# Revit family: Celite_City_Lavatório com Coluna Suspensa_20001
name_source: partatom
category: Plumbing Fixtures
revit_build: Autodesk Revit MEP 2014 (Build: 20131024_2115(x64)
units: mm (PartAtom-declared; Revit-internal decimal feet)

## types (4) — shared parameters
Assembly Code = D2010400
Celite: Categoria = Linhas completas
Celite: Código = 20001
Celite: Desenho Técnico = http://www.celite.com.br
Celite: Fabricante = Celite
Celite: Linha = City
Celite: Link do Produto = http://www.celite.com.br
Celite: Norma = ABNT NBR 15097-1: 2011 - Requisitos e métodos de ensaio
Celite: Produto = Louças
Celite: Tipo = Lavatórios com coluna
Celite: Versão = Autodesk Revit MEP 2014
Desenvolvido por = ofcdesk
Diâmetro Ponto de Esgoto = 40 mm
Manufacturer = Celite
Model = 20001
Raio Ponto de Esgoto = 20 mm
Selo de Qualidade ofcdesk = Standard
URL = http://www.celite.com.br
WFU = 2
zero-valued in all types: CWFU, Default Elevation, HWFU

## per-type parameters (varying)
| type | Celite: Cores Disponíveis | Celite: Descrição | Description | Tipo de coluna |
| Branca - 20001 | Branco | Lavatório com coluna suspensa cor branca (20001), linha City - Louças Celite | Lavatório com coluna suspensa cor branca (20001), linha City - Louças Celite | Celite_City_Coluna para Lavatório_20201 : Suspensa Branco - 20202 |
| Preta - 20001 | Preto | Lavatório com coluna suspensa cor preta (20001), linha City - Louças Celite | Lavatório com coluna suspensa cor preta (20001), linha City - Louças Celite | Celite_City_Coluna para Lavatório_20201 : Suspensa Preto - 20202 |
| Pergamon - 20001 | Pergamon | Lavatório com coluna suspensa cor pergamon (20001), linha City - Louças Celite | Lavatório com coluna suspensa cor pergamon (20001), linha City - Louças Celite | Celite_City_Coluna para Lavatório_20201 : Suspensa Pergamon - 20202 |
| Cinza prata - 20001 | Cinza prata | Lavatório com coluna suspensa cor cinza prata (20001), linha City - Louças Celite | Lavatório com coluna suspensa cor cinza prata (20001), linha City - Louças Celite | Celite_City_Coluna para Lavatório_20201 : Suspensa Cinza prata - 20202 |

## geometry (parser evidence)
native form markers: Blend x2, Sweep x10
no freeform markers — native parametric forms only
